# Revit family: HL_RU_Floor drain_HL90Prblue-3020-B-221019
name_source: partatom
category: Instalační zařizovací předměty
units: mm (PartAtom-declared; Revit-internal decimal feet)

## family parameters
Bod výpočtu místnosti = Ano
Kóta kulaté spojky = Použít průměr
Nadpis OmniClass = Deck Waste Water Drains
Ořezat dutým tvarem při načtení = Ne
Sdílené = Ano
Typ dílu = Normální
Vždy vertikální = Ano
Založené na pracovní rovině = Ne
Číslo OmniClass = 23.70.50.21.24.14

## types (1)
- HL90Prblue-3020
    EAN = 9003076050529
    Indexovaná poznámka = HL90Prblue-3020
    Komentáře k typům = Трап для внутренних помещений с горизонтальным выпуском DN40/50 с "СУХИМ" сифоном и надставным элементом для вклеивания керамической плитки 132х132 мм/112х112 мм
    Model = HL90Prblue-3020
    Popis = Трапы для внутренних помещений
    Přípoj CW = Ne
    Přípoj HW = Ne
    Přípoj odpadních dílů = Ano
    Přípoj ventilace = Ne
    URL = https://www.hutterer-lechner.com
    Výchozí výška = 0 mm  [stored 0 ft]
    Výrobce = HL Hutterer & Lechner GmbH
    ВЕС = 0,765 [kg]
    ВЫСОТА МОНТАЖА = 89 mm
    МАКСИМАЛЬНАЯ НАГРУЗКА КЛАССА = K3 - 300 kg
    МАТЕРИАЛ = PP, ABS, Edelstahl
    НАСАДКА = 10-80mm/132x132mm
    НОМИНАЛЬНЫЙ ДИАМЕТР = 50 mm
    НОРМЫ = EN 1253
    ПРОИЗВОДИТЕЛЬНОСТЬ = 0,5 l/s
    ПРОПУСКНАЯ СПОСОБНОСТЬ = 0.4 L/s
    РАЗМЕР = DN40/50
    РЕШЁТКА = Edelstahl 112x112 (104x104X12)

note: [stored X ft] marks values corroborated as IEEE doubles in the binary element streams (Revit-internal decimal feet)

## geometry (parser evidence)
native form markers: Sweep x18
no freeform markers — native parametric forms only
